# Revit family: Drain_Pit_Zurn_Z1739
name_source: partatom
category: Plumbing Fixtures
units: mm (PartAtom-declared; Revit-internal decimal feet)

## family parameters
Cut with Voids When Loaded = No
Host = Face
Maintain Annotation Orientation = No
OmniClass Number = 23.45.55.21
OmniClass Title = Drains (Wastes)
Part Type = Normal
Room Calculation Point = No
Round Connector Dimension = Use Diameter
Shared = No

## types (4) — shared parameters
Assembly Code = D2030300
CW Connection = No
CWFU = 1
Default Elevation = 48 "
Description = Pit Drain
Dim 'B' = 13 "
Dim 'C' = 7.625 "
Dim 'E' = 7.5 "
Dim 'E2' = 3.75 "
Dim 'F' = 12.75 "
Dim 'G' = 11 "
Dim 'H' = 9.25 "
HW Connection = No
HWFU = 1
Manufacturer = Zurn
Manufacturer Brand = Zurn Water, LLC
Modified Date = 9/11/2025
Product Documentation Link = http://www.zurn.com
Product Page URL = http://www.zurn.com
Product data url = https://bimobject.com
URL = http://www.zurn.com
Vent Connection = Yes
Waste Connection = No
zero-valued in all types: WFU

## per-type parameters (varying)
| type | Dim 'A' | Dim 'A1' | Dim 'A2' | Dim 'D' | Dim 'x' | Main Material | Model | Nominal Diameter | Product Weight (lbs) |
| Z1739-3 inch Butt-weld Outlet | 3.068 " | 1.534 " | 1.75 " | 1.534 " | 1.409 " | Steel - Zurn - Stainless - Type 304 | Z1739-3BW | 3 " | 0 |
| Z1739-4 inch Butt-weld Outlet | 4.026 " | 2.013 " | 2.25 " | 2.013 " | 1.888 " | Steel - Zurn - Stainless - Type 304 | Z1739-4BW | 4 " | 50 |
| ZM1739-3 inch Butt-weld Outlet | 3.068 " | 1.534 " | 1.75 " | 1.534 " | 1.409 " | Steel - Zurn- Stainless - Type - 316 | Z1739-3BW | 3 " | 0 |
| ZM1739-4 inch Butt-weld Outlet | 4.026 " | 2.013 " | 2.25 " | 2.013 " | 1.888 " | Steel - Zurn- Stainless - Type - 316 | Z1739-4BW | 4 " | 0 |

## geometry (parser evidence)
native form markers: Sweep x4
no freeform markers — native parametric forms only
